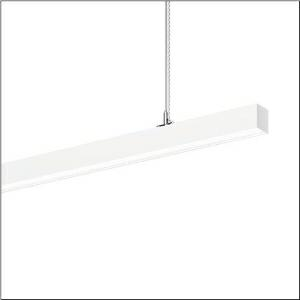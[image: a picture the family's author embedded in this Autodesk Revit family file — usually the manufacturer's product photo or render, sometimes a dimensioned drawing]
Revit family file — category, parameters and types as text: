
# Revit family: silica_r__21_51mx30dc39wb_5262
name_source: partatom
category: Lighting Fixtures
units: mm (PartAtom-declared; Revit-internal decimal feet)

## family parameters
Cut with Voids When Loaded = No
Host = Face
Light Source = No
Part Type = Normal
Room Calculation Point = No
Round Connector Dimension = Use Diameter
Shared = No

## types (1)
- --- (1 x LED, 10520 lm, 68.3 W, 3000K)
    Apparent Load = 68 VA
    CIE Flux Codes = 47 79 96 57 100
    Color Rendering = 80
    Color Temperature = 3000K
    Default Elevation = 1800 mm
    Description = Silica® 21, office luminaire, primary optical cover: cover, of PMMA, opal, light emission: direct/indirect distribution, primary light characteristic: symmetric, installation type: suspended mounting, LED, rated luminous flux: 10.520lm, luminous efficacy: 154lm/W, light colour: 830, colour temperature: 3000K, with terminal, 3+2-pole, max. 2.5mm², mains connection: 220..240V, AC, 50/60Hz, rated input power: 68.3W, luminaire housing, of aluminium, traffic white (RAL 9016), length: 3.004mm, width: 53mm, height: 53mm, protection rating (complete): IP20, insulation class (complete): insulation class I (protective earthing), certification: CE, permissible operating ambient temperature: 0..+35°C, standard: EN 50419, packaging unit: 1 piece
    Height = 53 mm
    Lamp = 1 x LED
    Lamp Light Flux = 10520 lm
    Lamp Power = 68.3 W
    Lamp count = 1
    Length = 3004 mm
    Luminous efficacy = 154 lm/W
    Manufacturer = Siteco
    ModVariant = No
    Model = 51MX30DC39WB
    Mounting Place = Ceiling
    Mounting Type = Pendant
    Number of Poles = 1
    OnlyDefault = Yes
    Power Factor = 1
    Product Name = Silica® 21
    Product group = office luminaire | ceiling pendant
    ProductGroupID = 905
    Protection Class = Protection class I
    Protection Degree = IP 20
    RLX_Detail_Level = 1
    RlxData = <blob elided: 21301 chars, md5=8dba9456>
    Socket = socket
    Standby Power = 0 W
    System Light Flux = 10520 lm
    System Power = 68 W
    Type Comments = factory setting: luminous flux: 100 % | dim-lin: 254 | 233 mA
    Type Image = l_1251642.jpg
    URL = http://relux.com
    VarID = @adj_025793
    Voltage = 0 V
    Weight = 0.00 kg
    Width = 53 mm

## geometry (parser evidence)
native form markers: Blend x4, Sweep x12
no freeform markers — native parametric forms only
